# Revit family: IS_Iom_A7651_BIM_NL
name_source: partatom
category: Plumbing Fixtures
units: mm (PartAtom-declared; Revit-internal decimal feet)

## family parameters
Always vertical = No
Cut with Voids When Loaded = No
OmniClass Number = 23.45.05.14.21.11
OmniClass Title = Bath/Shower Units
Part Type = Normal
Room Calculation Point = No
Round Connector Dimension = Use Diameter
Shared = No
Work Plane-Based = No

## types (5) — shared parameters
Accessories = http://www.idealstandard.nl
Afmetingen = 48 x 370 x 60 mm
AfstandsEenheid = Millimeter
AreaUnits = millimetres
AssetType = Fixed
Auteur = Ideal Standard
BIMObjectName = IS_IdealStandard_SanitaryAccessories_IOM_A7651
BIMobject category = Sanitary: Toilet Accssories
BIMobject main category = Sanitary
BIMobject main category code = Sanitary
Beschrijvinggarantie = Herstellergarantie
Bestanddelen = http://www.idealstandard.nl
BimObjectNaam = IS_IdealStandard_SanitaryAccessories_IOM_A7651
Brand = Ideal Standard
Brand url = www.idealstandard.co.uk
Breedte = 48
Category = Plumbing
Classification = Sanitary
ConnectionType = Plumbing
CurrencyUnit = €
CurrentRevision = 1
Date of publishing = 24/01/2023
Diepte = 371 mm
DurationUnit = Years
DuurEenheid = Jahr
Edition number = 2
ElementType = Sanitary Accessories
Garantieunits = Jahre
GemaaktOp = 24/01/2023
Help = http://www.idealstandard.nl
Hoogte = 59.0902194976807
IFC Classification = IfcFurnitureType
IfcExportAs = IfcFurnitureType
IfcExportType = TOWELRAIL
Installatieinstructies = http://www.idealstandard.nl
Installation instructions = http://www.idealstandard.nl
InstallationInstructions = http://www.idealstandard.nl
Lengte = 371 mm
LinearUnits = millimeters
MaintenanceInformation = http://www.idealstandard.nl
Manufacturer = Ideal Standard
Manufacturer name = Ideal standard test account
ManufacturerURL = http://www.idealstandard.nl
Materiaal = Messing&Stahl
Material = brass&steel
Material main = brass&steel
Merk = Ideal Standard
ModelReference = IOM Single Tower Rail 370
NBS Reference Code = 45-35-72/372
NBS Reference Description = Towel rails
Name = SanitaryAccessories_IOM_A7651_IdealStandard
NettWeight = 0.45
Nettogewicht = 0.45
NominalDepth = 371 mm
NominalHeight = 59 mm
NominalLength = 371 mm
NominalWidth = 48 mm
OppervlakteAfmeting = Millimeter
OppervlakteEenheid = Millimeter
PredefinedType = Sanitary Accessories
Product Guid = 2d679e64-5759-4658-991c-d079c947272d
Product SKU = A7651
Product certification = http://www.idealstandard.nl
Product data url = https://bimobject.com
Product family = IOM
Product group = Accessories
Product name = IOM TW/RAIL 370 SINGLE CHROME
Product url = http://www.idealstandard.nl
ProductInformation = http://www.idealstandard.nl
Productinformatie = http://www.idealstandard.nl
QR code = http://bimobject.com
Revisie = 1
Shape = cilindrical
Size = 48 x 370 x 60 mm
Space = Internal
SpareParts = http://www.idealstandard.nl
Technical description = http://www.idealstandard.nl
Telefoonnummer = 077 355 08 08
Typeconnectie = Installation
UNSPSC Code = 30181500
URL = http://www.idealstandard.nl
Uniclass 1.4 Code = N14
Uniclass 1.4 Description = Accessories
Uniclass 2015 Code = Pr_40_20_76
Uniclass 2015 Name = Sanitary accessories
Uniclass2015Beschrijving = Sanitary accessories
Uniclass2015Code = Pr_40_20_76
Uniclass2015Referentie = Sanitary accessories
Uniclass2015Title = Sanitary accessories
Uniclass2015Version = V1.26
Uniformat II Code = C1030
Uniformat II Description = Fittings
Urlproducent = http://www.idealstandard.nl
ValutaEenheid = €
Versie = 1
Version = 1
VolumeUnits = Liters
Volumeunits = Liter
Vorm = Zylinder
WRASURL = https://www.wrasapprovals.co.uk
WarrantyDescription = Manufacturers Warranty
WarrantyDurationUnit = Years
Weight Net (Kg) = 0.45
Wisselstukken = http://www.idealstandard.nl
Youtube clip = https://www.youtube.com
zero-valued in all types: BrutoGewicht, Cost, Vervangingskosten

## per-type parameters (varying)
| type | Afwerking | Artikelnummer | Artikelomschrijving | BarCode | Color | Description | Features | Finish | GTIN code | Kleur | MainColor | Model | ModelNumber |
| A7651AA - IOM Single Tower Rail 370 - Chrome | Chrom | A7651AA | IOM Single Tower Rail 370 - Chrom | 4015413354127 | Chrome | IOM Single Tower Rail 370 - Chrome | Single Tower Rail 370 - Chrome | Chrome | 4015413354127 | Chrom | Chrome | A7651AA | A7651AA |
| A7651A2 - IOM Single Tower Rail 370 - Brushed Gold | Gebürstetes Gold | A7651A2 | IOM Single Tower Rail 370 – Gebürstetes Gold | 4015413354264 | Brushed Gold | IOM Single Tower Rail 370 - Brushed Gold | Single Tower Rail 370 - Brushed Gold | Brushed Gold | 4015413354264 | Gebürstetes Gold | Brushed Gold | A7651A2 | A7651A2 |
| A7651A5 - IOM Single Tower Rail 370 - Magnetic Grey | Magnetisches Grau | A7651A5 | IOM Single Tower Rail 370 – Magnetgrau | 4015413354271 | Magnetic Grey | IOM Single Tower Rail 370 - Magnetic Grey | Single Tower Rail 370 - Magnetic Grey | Magnetic Grey | 4015413354271 | Magnetisches Grau | Magnetic Grey | A7651A5 | A7651A5 |
| A7651GN - IOM Single Tower Rail 370 - Silver Storm | Silberner Sturm | A7651GN | IOM Single Tower Rail 370 - Silberner Sturm | 4015413354288 | Silver Storm | IOM Single Tower Rail 370 - Silver Storm | Single Tower Rail 370 - Silver Storm | Silver Storm | 4015413354288 | Silberner Sturm | Silver Storm | A7651GN | A7651AGN |
| A7651XG - IOM Single Tower Rail 370 - Silk Black | Seidenschwarz | A7651XG | IOM Single Tower Rail 370 - Seidenschwarz | 4015413354134 | Silk Black | IOM Single Tower Rail 370 - Silk Black | Single Tower Rail 370 - Silk Black | Silk Black | 4015413354134 | Seidenschwarz | Silk Black | A7651XG | A7651AXG |

## geometry (parser evidence)
native form markers: Sweep x4
no freeform markers — native parametric forms only
